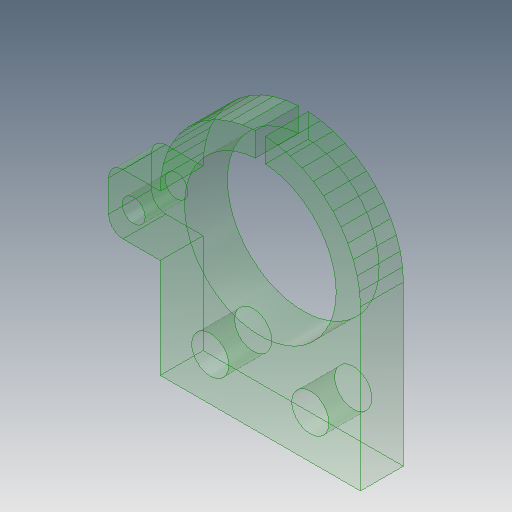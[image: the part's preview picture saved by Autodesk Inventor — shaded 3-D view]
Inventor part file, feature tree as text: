
AUTODESK INVENTOR PART (.ipt)
format: ipt  version: 2017 (Build 210142000, 142)  size: 202,240 bytes
history: native  units: mm
features: other x3, sketch x2
ambient origin geometry x8: Origin, YZ Plane, XZ Plane, XY Plane, X Axis, Y Axis, Z Axis, Center Point
bodies: Solid1 (feature_tree)
feature tree (5):
  other  "Left Bed Holder Upper.ipt"
  other  "Solid1::Left Bed Holder Upper.ipt"
  other  "TaggingFeature1"
  sketch  "Sketch1"  dims[d0=10.0mm]
  sketch  "Sketch3"
